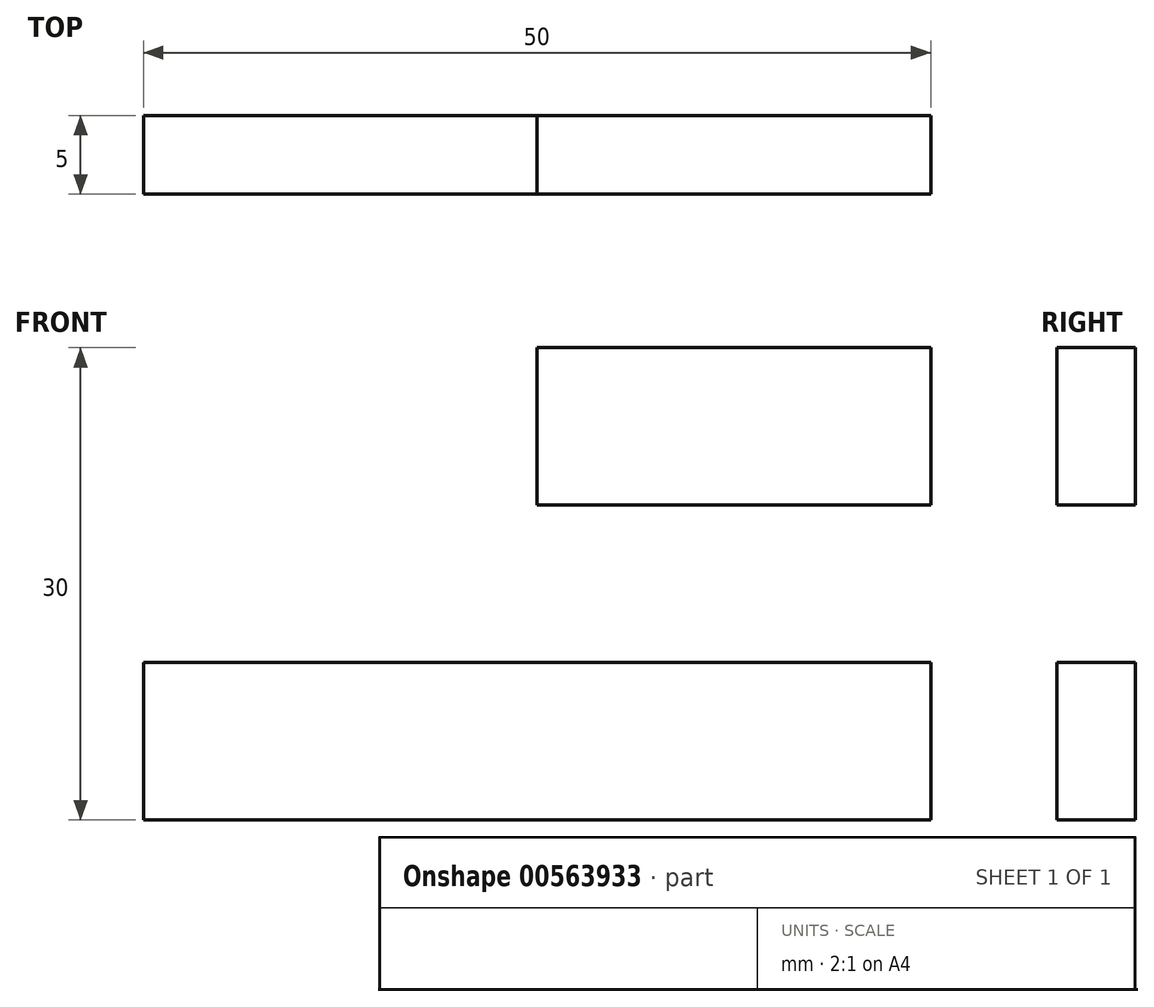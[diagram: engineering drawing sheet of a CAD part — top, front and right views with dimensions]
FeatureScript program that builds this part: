
annotation { "Feature Type Name" : "Feature", "Feature Type Description" : "" }
export const myFeature = defineFeature(function(context is Context, id is Id, definition is map)
    precondition{}
    {
        {
            var Q0;
            Q0=qCreatedBy(makeId("Front.planeOp"),FACE);
            var sketch = newSketch(context, id + "F0", { "sketchPlane" : qUnion([Q0])});
            skLineSegment(sketch, "E0.bottom", {"start": v(0, 0) * mm, "end": v(50, 0) * mm});
            skLineSegment(sketch, "E0.top", {"start": v(0, -10) * mm, "end": v(50, -10) * mm});
            skLineSegment(sketch, "E0.left", {"start": v(0, 0) * mm, "end": v(0, -10) * mm});
            skLineSegment(sketch, "E0.right", {"start": v(50, 0) * mm, "end": v(50, -10) * mm});
            skLineSegment(sketch, "E1.bottom", {"start": v(50, 0) * mm, "end": v(45, 0) * mm});
            skLineSegment(sketch, "E1.top", {"start": v(50, 10) * mm, "end": v(45, 10) * mm});
            skLineSegment(sketch, "E1.left", {"start": v(50, 0) * mm, "end": v(50, 10) * mm});
            skLineSegment(sketch, "E1.right", {"start": v(45, 0) * mm, "end": v(45, 10) * mm});
            skLineSegment(sketch, "E2.bottom", {"start": v(50, 10) * mm, "end": v(25, 10) * mm});
            skLineSegment(sketch, "E2.top", {"start": v(50, 20) * mm, "end": v(25, 20) * mm});
            skLineSegment(sketch, "E2.left", {"start": v(50, 10) * mm, "end": v(50, 20) * mm});
            skLineSegment(sketch, "E2.right", {"start": v(25, 10) * mm, "end": v(25, 20) * mm});
            skSolve(sketch);
        }
        {
            var Q0;
            Q0=makeQuery(id+"F0.imprint","IMPRINT",FACE,{"disambiguationData":[TD([[makeQuery(id+"F0.imprint","IMPRINT",EDGE,{"derivedFrom":sQuery(id+"F0.wireOp",EDGE,"E0.bottom")}),-1.0]])]});
            var Q1;
            Q1=makeQuery(id+"F0.imprint","IMPRINT",FACE,{"disambiguationData":[TD([[makeQuery(id+"F0.imprint","IMPRINT",EDGE,{"derivedFrom":sQuery(id+"F0.wireOp",EDGE,"E2.top")}),1.0]])]});
            var Q2;
            Q2=makeQuery(id+"F0.imprint","IMPRINT",FACE,{"disambiguationData":[TD([[makeQuery(id+"F0.imprint","IMPRINT",EDGE,{"derivedFrom":sQuery(id+"F0.wireOp",EDGE,"E1.bottom")}),-1.0]])]});
            extrude(context, id + "F1", {"entities" : qUnion([Q0, Q1, Q2]), "depth" : 5 * mm, "offsetDistance" : 25 * mm});
        }
    });
